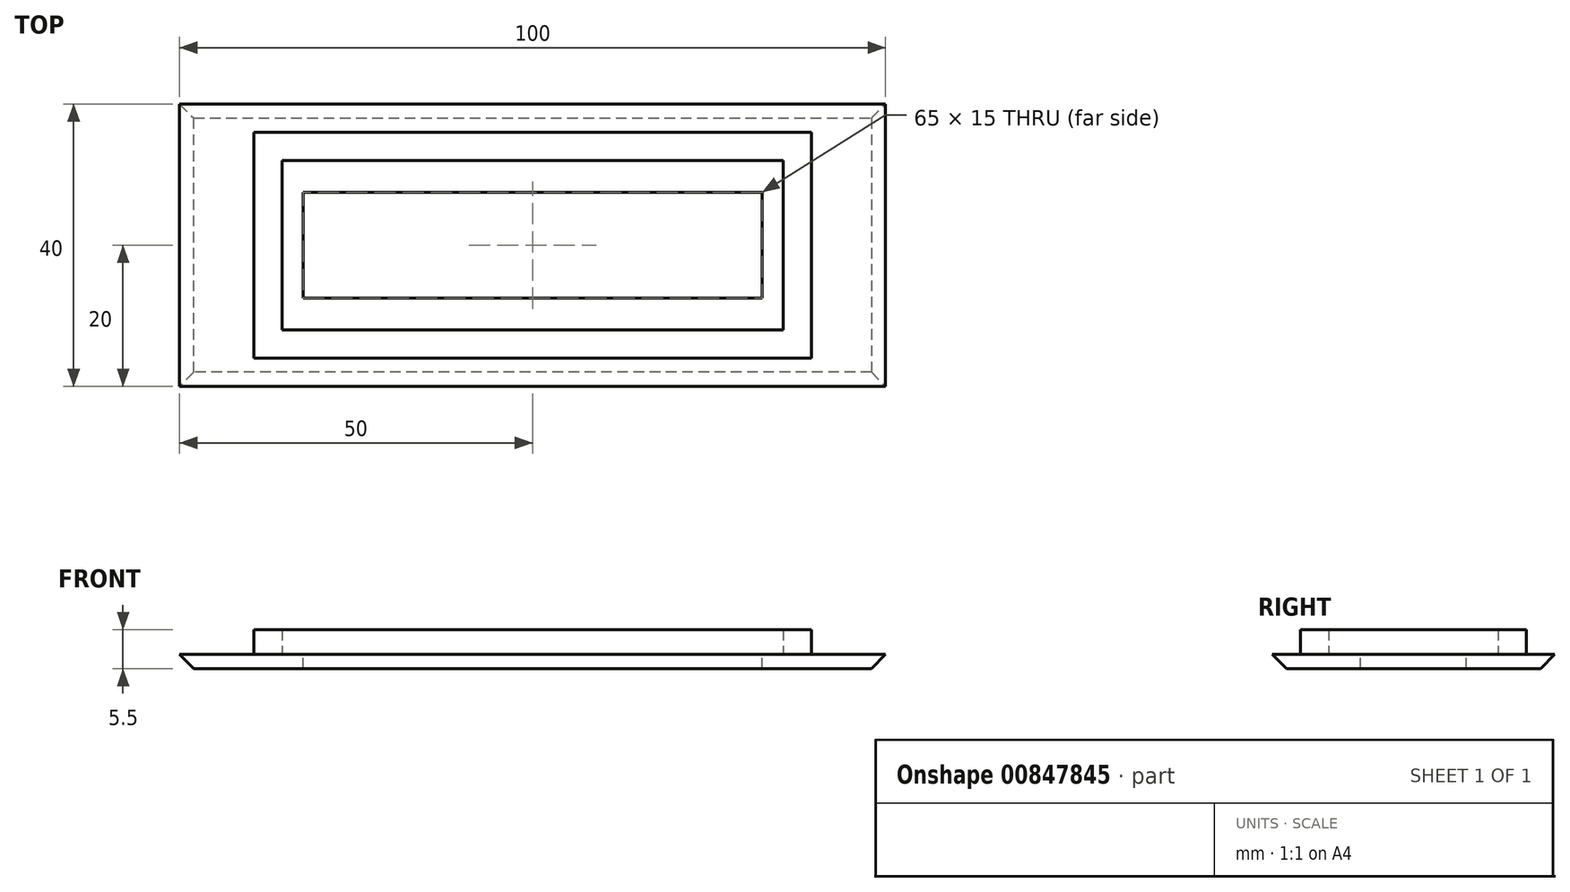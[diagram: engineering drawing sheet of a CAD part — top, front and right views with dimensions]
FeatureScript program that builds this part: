
annotation { "Feature Type Name" : "Feature", "Feature Type Description" : "" }
export const myFeature = defineFeature(function(context is Context, id is Id, definition is map)
    precondition{}
    {
        {
            var Q0;
            Q0=qCreatedBy(makeId("Top.planeOp"),FACE);
            var sketch = newSketch(context, id + "F0", { "sketchPlane" : qUnion([Q0])});
            skLineSegment(sketch, "E0.bottom", {"start": v(-50, 20) * mm, "end": v(50, 20) * mm});
            skLineSegment(sketch, "E0.top", {"start": v(-50, -20) * mm, "end": v(50, -20) * mm});
            skLineSegment(sketch, "E0.left", {"start": v(-50, 20) * mm, "end": v(-50, -20) * mm});
            skLineSegment(sketch, "E0.right", {"start": v(50, 20) * mm, "end": v(50, -20) * mm});
            skSolve(sketch);
        }
        {
            var Q0;
            Q0=makeQuery(id+"F0.imprint","IMPRINT",FACE,{"disambiguationData":[TD([[makeQuery(id+"F0.imprint","IMPRINT",EDGE,{"derivedFrom":sQuery(id+"F0.wireOp",EDGE,"E0.bottom")}),-1.0]])]});
            extrude(context, id + "F1", {"entities" : qUnion([Q0]), "depth" : 2 * mm, "offsetDistance" : 25 * mm});
        }
        {
            var Q0;
            Q0=makeQuery(id+"F1.opExtrude","CAP_FACE",FACE,{"disambiguationData":[OSD([sQuery(id+"F0.wireOp",EDGE,"E0.bottom"),sQuery(id+"F0.wireOp",EDGE,"E0.top"),sQuery(id+"F0.wireOp",EDGE,"E0.left"),sQuery(id+"F0.wireOp",EDGE,"E0.right")])],"isStart":false});
            var sketch = newSketch(context, id + "F2", { "sketchPlane" : qUnion([Q0])});
            skLineSegment(sketch, "E1.bottom", {"start": v(-35.5, 12) * mm, "end": v(35.5, 12) * mm});
            skLineSegment(sketch, "E1.top", {"start": v(-35.5, -12) * mm, "end": v(35.5, -12) * mm});
            skLineSegment(sketch, "E1.left", {"start": v(-35.5, 12) * mm, "end": v(-35.5, -12) * mm});
            skLineSegment(sketch, "E1.right", {"start": v(35.5, 12) * mm, "end": v(35.5, -12) * mm});
            skLineSegment(sketch, "E2.bottom", {"start": v(-39.5, 16) * mm, "end": v(39.5, 16) * mm});
            skLineSegment(sketch, "E2.top", {"start": v(-39.5, -16) * mm, "end": v(39.5, -16) * mm});
            skLineSegment(sketch, "E2.left", {"start": v(-39.5, 16) * mm, "end": v(-39.5, -16) * mm});
            skLineSegment(sketch, "E2.right", {"start": v(39.5, 16) * mm, "end": v(39.5, -16) * mm});
            skSolve(sketch);
        }
        {
            var Q0;
            Q0=makeQuery(id+"F2.imprint","IMPRINT",FACE,{"disambiguationData":[TD([[makeQuery(id+"F2.imprint","IMPRINT",EDGE,{"derivedFrom":sQuery(id+"F2.wireOp",EDGE,"E1.bottom")}),1.0]])]});
            extrude(context, id + "F3", {"entities" : qUnion([Q0]), "operationType" : NewBodyOperationType.ADD, "depth" : 3.5 * mm, "offsetDistance" : 25 * mm});
        }
        {
            var Q0;
            Q0=makeQuery(id+"F3.boolean.opBoolean","SPLIT",FACE,{"disambiguationData":[TD([makeQuery(id+"F3.opExtrude","SWEPT_FACE",FACE,{"disambiguationData":[OSD([sQuery(id+"F2.wireOp",EDGE,"E1.bottom")])]})])],"derivedFrom":makeQuery(id+"F1.opExtrude","CAP_FACE",FACE,{"disambiguationData":[OSD([sQuery(id+"F0.wireOp",EDGE,"E0.bottom"),sQuery(id+"F0.wireOp",EDGE,"E0.top"),sQuery(id+"F0.wireOp",EDGE,"E0.left"),sQuery(id+"F0.wireOp",EDGE,"E0.right")])],"isStart":false})});
            var sketch = newSketch(context, id + "F4", { "sketchPlane" : qUnion([Q0])});
            skLineSegment(sketch, "E3.bottom", {"start": v(-32.5, 7.5) * mm, "end": v(32.5, 7.5) * mm});
            skLineSegment(sketch, "E3.top", {"start": v(-32.5, -7.5) * mm, "end": v(32.5, -7.5) * mm});
            skLineSegment(sketch, "E3.left", {"start": v(-32.5, 7.5) * mm, "end": v(-32.5, -7.5) * mm});
            skLineSegment(sketch, "E3.right", {"start": v(32.5, 7.5) * mm, "end": v(32.5, -7.5) * mm});
            skSolve(sketch);
        }
        {
            var Q0;
            Q0=makeQuery(id+"F4.imprint","IMPRINT",FACE,{"disambiguationData":[TD([[makeQuery(id+"F4.imprint","IMPRINT",EDGE,{"derivedFrom":sQuery(id+"F4.wireOp",EDGE,"E3.bottom")}),-1.0]])]});
            extrude(context, id + "F5", {"entities" : qUnion([Q0]), "operationType" : NewBodyOperationType.REMOVE, "endBound" : BoundingType.UP_TO_NEXT, "oppositeDirection" : true, "depth" : 25 * mm, "offsetDistance" : 25 * mm});
        }
        {
            var Q0;
            Q0=makeQuery(id+"F5.boolean.opBoolean","COPY",EDGE,{"derivedFrom":makeQuery(id+"F5.opExtrude","CAP_EDGE",EDGE,{"disambiguationData":[OSD([sQuery(id+"F4.wireOp",EDGE,"E3.right")])],"isStart":false})});
            var Q1;
            Q1=makeQuery(id+"F5.boolean.opBoolean","COPY",EDGE,{"derivedFrom":makeQuery(id+"F5.opExtrude","CAP_EDGE",EDGE,{"disambiguationData":[OSD([sQuery(id+"F4.wireOp",EDGE,"E3.bottom")])],"isStart":false})});
            var Q2;
            Q2=makeQuery(id+"F5.boolean.opBoolean","COPY",EDGE,{"derivedFrom":makeQuery(id+"F5.opExtrude","CAP_EDGE",EDGE,{"disambiguationData":[OSD([sQuery(id+"F4.wireOp",EDGE,"E3.left")])],"isStart":false})});
            var Q3;
            Q3=makeQuery(id+"F5.boolean.opBoolean","COPY",EDGE,{"derivedFrom":makeQuery(id+"F5.opExtrude","CAP_EDGE",EDGE,{"disambiguationData":[OSD([sQuery(id+"F4.wireOp",EDGE,"E3.top")])],"isStart":false})});
            var Q4;
            Q4=makeQuery(id+"F1.opExtrude","CAP_EDGE",EDGE,{"disambiguationData":[OSD([sQuery(id+"F0.wireOp",EDGE,"E0.bottom")])],"isStart":true});
            var Q5;
            Q5=makeQuery(id+"F1.opExtrude","CAP_EDGE",EDGE,{"disambiguationData":[OSD([sQuery(id+"F0.wireOp",EDGE,"E0.right")])],"isStart":true});
            var Q6;
            Q6=makeQuery(id+"F1.opExtrude","CAP_EDGE",EDGE,{"disambiguationData":[OSD([sQuery(id+"F0.wireOp",EDGE,"E0.top")])],"isStart":true});
            var Q7;
            Q7=makeQuery(id+"F1.opExtrude","CAP_EDGE",EDGE,{"disambiguationData":[OSD([sQuery(id+"F0.wireOp",EDGE,"E0.left")])],"isStart":true});
            chamfer(context, id + "F6", {"entities" : qUnion([Q0, Q1, Q2, Q3, Q4, Q5, Q6, Q7]), "width" : 2 * mm, "tangentPropagation" : true});
        }
    });
